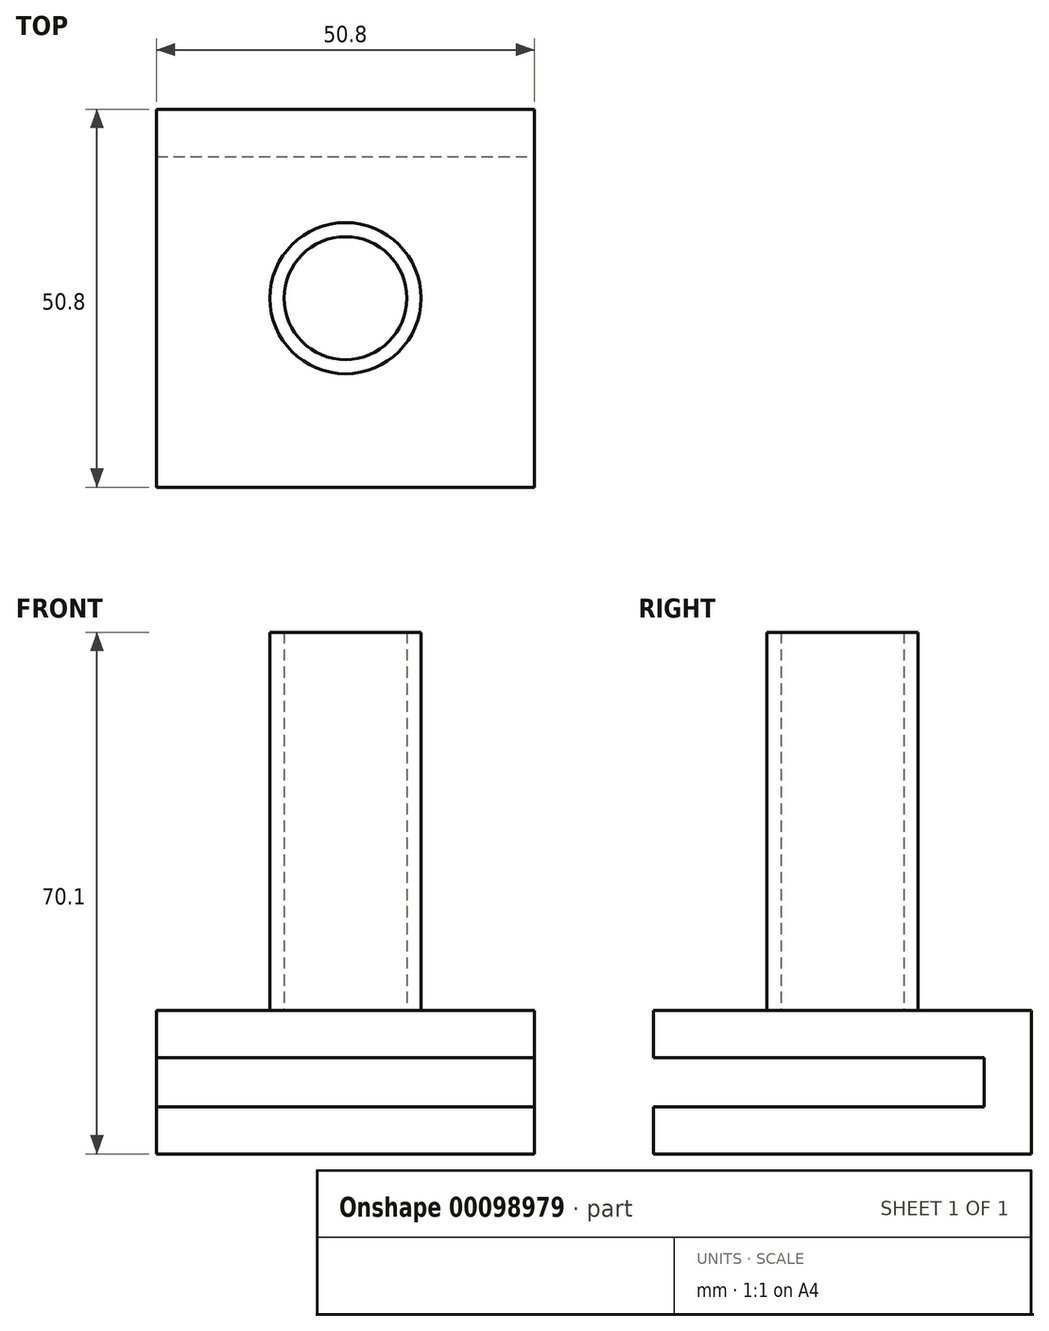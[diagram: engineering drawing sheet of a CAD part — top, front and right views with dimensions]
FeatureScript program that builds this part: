
annotation { "Feature Type Name" : "Feature", "Feature Type Description" : "" }
export const myFeature = defineFeature(function(context is Context, id is Id, definition is map)
    precondition{}
    {
        {
            var Q0;
            Q0=qCreatedBy(makeId("Top.planeOp"),FACE);
            var sketch = newSketch(context, id + "F0", { "sketchPlane" : qUnion([Q0])});
            skLineSegment(sketch, "E0.bottom", {"start": v(25.4, 25.4) * mm, "end": v(-25.4, 25.4) * mm});
            skLineSegment(sketch, "E0.top", {"start": v(25.4, -25.4) * mm, "end": v(-25.4, -25.4) * mm});
            skLineSegment(sketch, "E0.left", {"start": v(25.4, 25.4) * mm, "end": v(25.4, -25.4) * mm});
            skLineSegment(sketch, "E0.right", {"start": v(-25.4, 25.4) * mm, "end": v(-25.4, -25.4) * mm});
            skPoint(sketch, "E0.middle", {"position": v(0, 0) * mm});
            skSolve(sketch);
        }
        {
            var Q0;
            Q0 = qSketchRegion(id + "F0", true);
            extrude(context, id + "F1", {"entities" : qUnion([Q0]), "depth" : 6.35 * mm});
        }
        {
            var Q0;
            Q0=makeQuery(id+"F1.opExtrude","CAP_FACE",FACE,{"disambiguationData":[OSD([sQuery(id+"F0.wireOp",EDGE,"E0.bottom"),sQuery(id+"F0.wireOp",EDGE,"E0.top"),sQuery(id+"F0.wireOp",EDGE,"E0.left"),sQuery(id+"F0.wireOp",EDGE,"E0.right")])],"isStart":false});
            var sketch = newSketch(context, id + "F2", { "sketchPlane" : qUnion([Q0])});
            skLineSegment(sketch, "E1.bottom", {"start": v(-25.4, 25.4) * mm, "end": v(25.4, 25.4) * mm});
            skLineSegment(sketch, "E1.top", {"start": v(-25.4, 19.05) * mm, "end": v(25.4, 19.05) * mm});
            skLineSegment(sketch, "E1.left", {"start": v(-25.4, 25.4) * mm, "end": v(-25.4, 19.05) * mm});
            skLineSegment(sketch, "E1.right", {"start": v(25.4, 25.4) * mm, "end": v(25.4, 19.05) * mm});
            skSolve(sketch);
        }
        {
            var Q0;
            Q0 = qSketchRegion(id + "F2", true);
            extrude(context, id + "F3", {"entities" : qUnion([Q0]), "operationType" : NewBodyOperationType.ADD, "depth" : 6.6 * mm});
        }
        {
            var Q0;
            Q0=makeQuery(id+"F3.opExtrude","CAP_FACE",FACE,{"disambiguationData":[OSD([sQuery(id+"F2.wireOp",EDGE,"E1.bottom"),sQuery(id+"F2.wireOp",EDGE,"E1.top"),sQuery(id+"F2.wireOp",EDGE,"E1.left"),sQuery(id+"F2.wireOp",EDGE,"E1.right")])],"isStart":false});
            var sketch = newSketch(context, id + "F4", { "sketchPlane" : qUnion([Q0])});
            skLineSegment(sketch, "E2.bottom", {"start": v(-25.4, 25.4) * mm, "end": v(25.4, 25.4) * mm});
            skLineSegment(sketch, "E2.top", {"start": v(-25.4, -25.4) * mm, "end": v(25.4, -25.4) * mm});
            skLineSegment(sketch, "E2.left", {"start": v(-25.4, 25.4) * mm, "end": v(-25.4, -25.4) * mm});
            skLineSegment(sketch, "E2.right", {"start": v(25.4, 25.4) * mm, "end": v(25.4, -25.4) * mm});
            skSolve(sketch);
        }
        {
            var Q0;
            Q0 = qSketchRegion(id + "F4", true);
            extrude(context, id + "F5", {"entities" : qUnion([Q0]), "operationType" : NewBodyOperationType.ADD, "depth" : 6.35 * mm});
        }
        {
            var Q0;
            Q0=makeQuery(id+"F5.opExtrude","CAP_FACE",FACE,{"disambiguationData":[OSD([sQuery(id+"F4.wireOp",EDGE,"E2.bottom"),sQuery(id+"F4.wireOp",EDGE,"E2.top"),sQuery(id+"F4.wireOp",EDGE,"E2.left"),sQuery(id+"F4.wireOp",EDGE,"E2.right")])],"isStart":false});
            var sketch = newSketch(context, id + "F6", { "sketchPlane" : qUnion([Q0])});
            skCircle(sketch, "E3", {"center": v(0, 0) * mm, "radius": 10.16 * mm});
            skCircle(sketch, "E4", {"center": v(0, 0) * mm, "radius": 8.26 * mm});
            skSolve(sketch);
        }
        {
            var Q0;
            Q0 = qSketchRegion(id + "F6", true);
            extrude(context, id + "F7", {"entities" : qUnion([Q0]), "operationType" : NewBodyOperationType.ADD, "depth" : 50.8 * mm});
        }
    });
